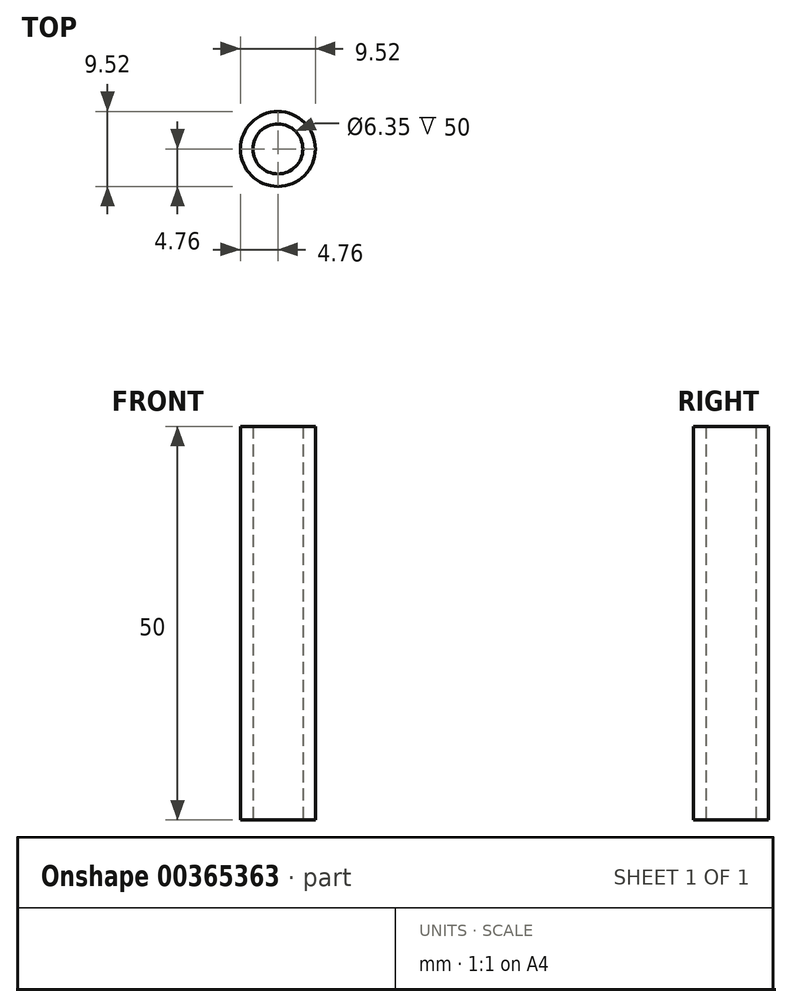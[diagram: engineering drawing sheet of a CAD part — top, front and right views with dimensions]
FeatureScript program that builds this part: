
annotation { "Feature Type Name" : "Feature", "Feature Type Description" : "" }
export const myFeature = defineFeature(function(context is Context, id is Id, definition is map)
    precondition{}
    {
        {
            var Q0;
            Q0=qCreatedBy(makeId("Top.planeOp"),FACE);
            var sketch = newSketch(context, id + "F0", { "sketchPlane" : qUnion([Q0])});
            skCircle(sketch, "E0", {"center": v(0, 0) * mm, "radius": 4.76 * mm});
            skCircle(sketch, "E1", {"center": v(0, 0) * mm, "radius": 3.17 * mm});
            skSolve(sketch);
        }
        {
            var Q0;
            Q0=qSketchRegion(id+"F0",true);
            extrude(context, id + "F1", {"entities" : qUnion([Q0]), "depth" : 50 * mm});
        }
    });
